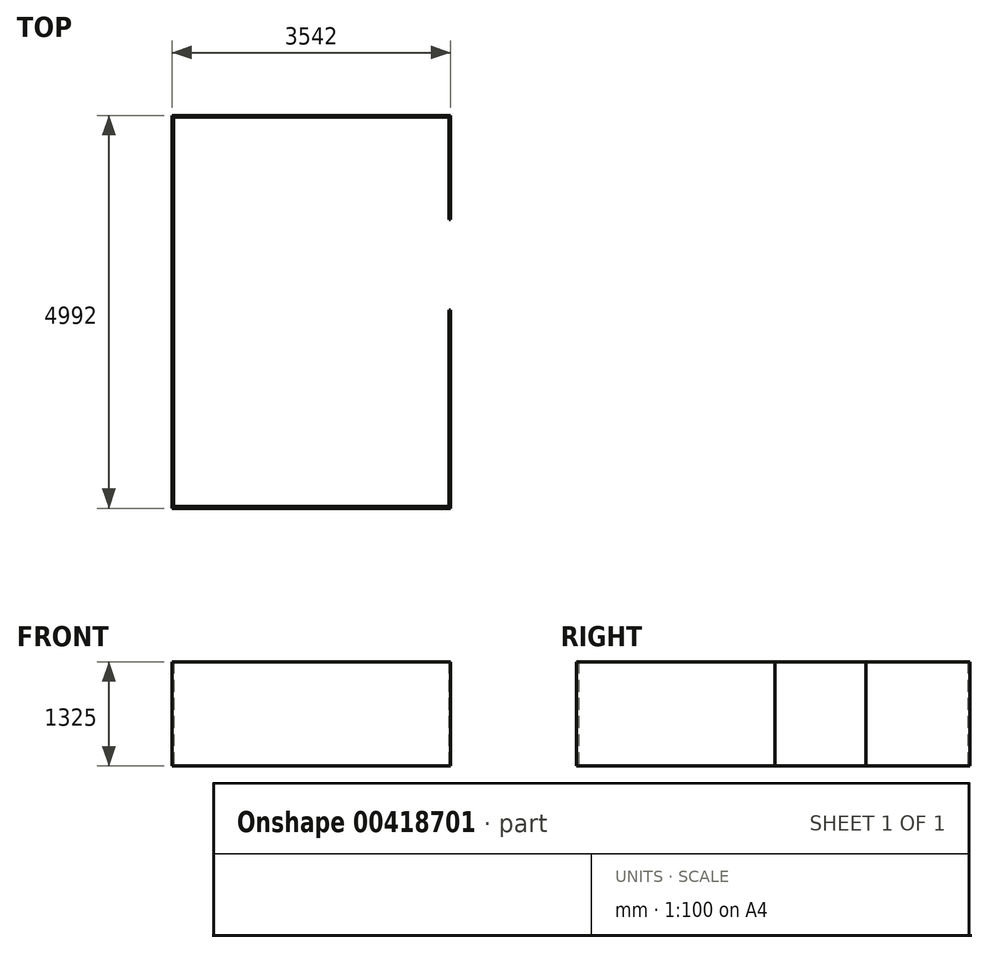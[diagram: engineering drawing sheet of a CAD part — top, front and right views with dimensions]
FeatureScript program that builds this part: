
annotation { "Feature Type Name" : "Feature", "Feature Type Description" : "" }
export const myFeature = defineFeature(function(context is Context, id is Id, definition is map)
    precondition{}
    {
        {
            var Q0;
            Q0=qCreatedBy(makeId("Top.planeOp"),FACE);
            var sketch = newSketch(context, id + "F0", { "sketchPlane" : qUnion([Q0])});
            skLineSegment(sketch, "E0", {"start": v(-1750, 2475) * mm, "end": v(-1750, -2475) * mm});
            skLineSegment(sketch, "E1", {"start": v(1750, -2475) * mm, "end": v(1750, 25) * mm});
            skLineSegment(sketch, "E2", {"start": v(-1750, 2475) * mm, "end": v(1750, 2475) * mm});
            skLineSegment(sketch, "E3", {"start": v(1750, 2475) * mm, "end": v(1750, 1175) * mm});
            skLineSegment(sketch, "E4.MirrorCS", {"start": v(-1750, -2475) * mm, "end": v(1750, -2475) * mm});
            skLineSegment(sketch, "E5.0", {"start": v(1771, 2496) * mm, "end": v(1771, 1175) * mm});
            skLineSegment(sketch, "E5.1", {"start": v(1771, -2496) * mm, "end": v(1771, 25) * mm});
            skLineSegment(sketch, "E5.2", {"start": v(-1771, -2496) * mm, "end": v(1771, -2496) * mm});
            skLineSegment(sketch, "E5.3", {"start": v(-1771, 2496) * mm, "end": v(-1771, -2496) * mm});
            skLineSegment(sketch, "E5.4", {"start": v(-1771, 2496) * mm, "end": v(1771, 2496) * mm});
            skLineSegment(sketch, "E6", {"start": v(1750, 1175) * mm, "end": v(1771, 1175) * mm});
            skLineSegment(sketch, "E7", {"start": v(1750, 25) * mm, "end": v(1771, 25) * mm});
            skSolve(sketch);
        }
        {
            var Q0;
            Q0 = qSketchRegion(id + "F0", true);
            extrude(context, id + "F1", {"entities" : qUnion([Q0]), "depth" : 1150 * mm, "offsetDistance" : 25 * mm, "hasSecondDirection" : true, "secondDirectionOppositeDirection" : true, "secondDirectionDepth" : 175 * mm});
        }
    });
